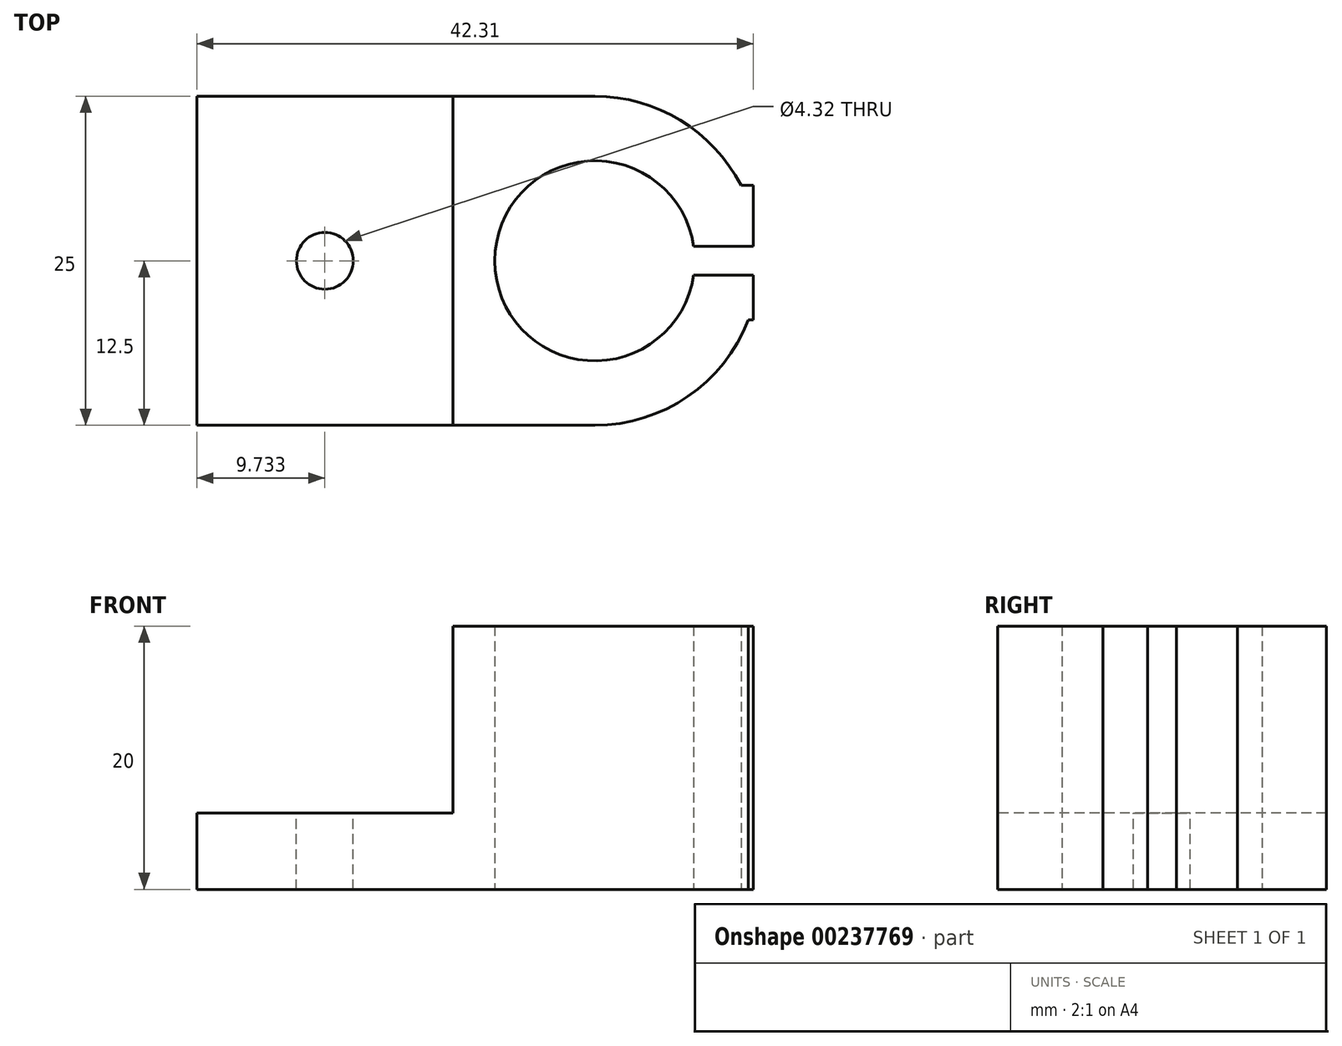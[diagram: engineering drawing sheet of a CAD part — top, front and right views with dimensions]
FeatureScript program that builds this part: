
annotation { "Feature Type Name" : "Feature", "Feature Type Description" : "" }
export const myFeature = defineFeature(function(context is Context, id is Id, definition is map)
    precondition{}
    {
        {
            var Q0;
            Q0=qCreatedBy(makeId("Top.planeOp"),FACE);
            var sketch = newSketch(context, id + "F0", { "sketchPlane" : qUnion([Q0])});
            skArc(sketch, "E0", {"start": v(7.52, 1.1) * mm, "mid": v(-7.6, 0) * mm, "end": v(7.52, -1.1) * mm});
            skArc(sketch, "E1", {"start": v(0, -12.5) * mm, "mid": v(7.07, -10.3) * mm, "end": v(11.66, -4.5) * mm});
            skLineSegment(sketch, "E2.left", {"start": v(-48.25, 4.5) * mm, "end": v(-48.25, -4.5) * mm, "construction": true});
            skLineSegment(sketch, "E2.right", {"start": v(-10.79, 4.5) * mm, "end": v(-10.79, -4.5) * mm, "construction": true});
            skLineSegment(sketch, "E3", {"start": v(0, 0) * mm, "end": v(-10.79, 0) * mm, "construction": true});
            skLineSegment(sketch, "E4", {"start": v(0, 12.5) * mm, "end": v(-30.25, 12.5) * mm});
            skLineSegment(sketch, "E5", {"start": v(-30.25, 12.5) * mm, "end": v(-30.25, -4.5) * mm});
            skPoint(sketch, "E5.endSnap0", {"position": v(-29.52, -4.5) * mm});
            skLineSegment(sketch, "E6", {"start": v(-10.79, 4.5) * mm, "end": v(-10.79, -4.5) * mm});
            skLineSegment(sketch, "E7", {"start": v(-30.25, -4.5) * mm, "end": v(-30.25, -12.5) * mm});
            skLineSegment(sketch, "E8", {"start": v(-30.25, -12.5) * mm, "end": v(0, -12.5) * mm});
            skLineSegment(sketch, "E9", {"start": v(11.11, 5.73) * mm, "end": v(12.06, 5.73) * mm});
            skLineSegment(sketch, "E10", {"start": v(12.06, 5.73) * mm, "end": v(12.06, 1.1) * mm});
            skLineSegment(sketch, "E11", {"start": v(12.06, 1.1) * mm, "end": v(7.52, 1.1) * mm});
            skLineSegment(sketch, "E12", {"start": v(7.52, -1.1) * mm, "end": v(12.06, -1.1) * mm});
            skLineSegment(sketch, "E13", {"start": v(12.06, -1.1) * mm, "end": v(12.06, -4.5) * mm});
            skLineSegment(sketch, "E14", {"start": v(12.06, -4.5) * mm, "end": v(11.66, -4.5) * mm});
            skArc(sketch, "E15.trimOffspring", {"start": v(11.11, 5.73) * mm, "mid": v(6.5, 10.67) * mm, "end": v(0, 12.5) * mm});
            skLineSegment(sketch, "E16", {"start": v(-10.79, 4.5) * mm, "end": v(-10.79, 12.5) * mm});
            skLineSegment(sketch, "E17", {"start": v(-10.79, -4.5) * mm, "end": v(-10.79, -12.5) * mm});
            skSolve(sketch);
        }
        {
            var Q0;
            Q0=makeQuery(id+"F0.imprint","IMPRINT",FACE,{"disambiguationData":[TD([[makeQuery(id+"F0.imprint","IMPRINT",EDGE,{"derivedFrom":sQuery(id+"F0.wireOp",EDGE,"E0")}),-1.0]])]});
            extrude(context, id + "F1", {"entities" : qUnion([Q0]), "depth" : 20 * mm});
        }
        {
            var Q0;
            {var subQ0=sQuery(id+"F0.wireOp",EDGE,"E5");Q0=makeQuery(id+"F0.imprint","IMPRINT",FACE,{"disambiguationData":[TD([[makeQuery(id+"F0.imprint","IMPRINT",EDGE,{"derivedFrom":subQ0}),1.0]])]});}
            var Q1;
            Q1=makeQuery(id+"F0.imprint","IMPRINT",FACE,{"disambiguationData":[TD([[makeQuery(id+"F0.imprint","IMPRINT",EDGE,{"derivedFrom":sQuery(id+"F0.wireOp",EDGE,"9WJQLeq8-gHu1-3Nqd-rDEh-Rfgkn3N6eF2B")}),1.0]])]});
            extrude(context, id + "F2", {"entities" : qUnion([Q0, Q1]), "operationType" : NewBodyOperationType.ADD, "depth" : 5.8 * mm});
        }
        {
            var Q0;
            Q0=makeQuery(id+"F2.opExtrude","CAP_FACE",FACE,{"disambiguationData":[OSD([sQuery(id+"F0.wireOp",EDGE,"E4"),sQuery(id+"F0.wireOp",EDGE,"E5"),sQuery(id+"F0.wireOp",EDGE,"E6"),sQuery(id+"F0.wireOp",EDGE,"E7"),sQuery(id+"F0.wireOp",EDGE,"E8"),sQuery(id+"F0.wireOp",EDGE,"E16"),sQuery(id+"F0.wireOp",EDGE,"E17")])],"isStart":false});
            var sketch = newSketch(context, id + "F3", { "sketchPlane" : qUnion([Q0])});
            skCircle(sketch, "E18", {"center": v(-20.52, 0) * mm, "radius": 2.16 * mm});
            skPoint(sketch, "E18.centerSnap0", {"position": v(-20.52, 12.5) * mm});
            skPoint(sketch, "E18.centerSnap1", {"position": v(-30.25, 0) * mm});
            skSolve(sketch);
        }
        {
            var Q0;
            Q0=qSketchRegion(id+"F3",true);
            extrude(context, id + "F4", {"entities" : qUnion([Q0]), "operationType" : NewBodyOperationType.REMOVE, "oppositeDirection" : true, "depth" : 25 * mm});
        }
    });
